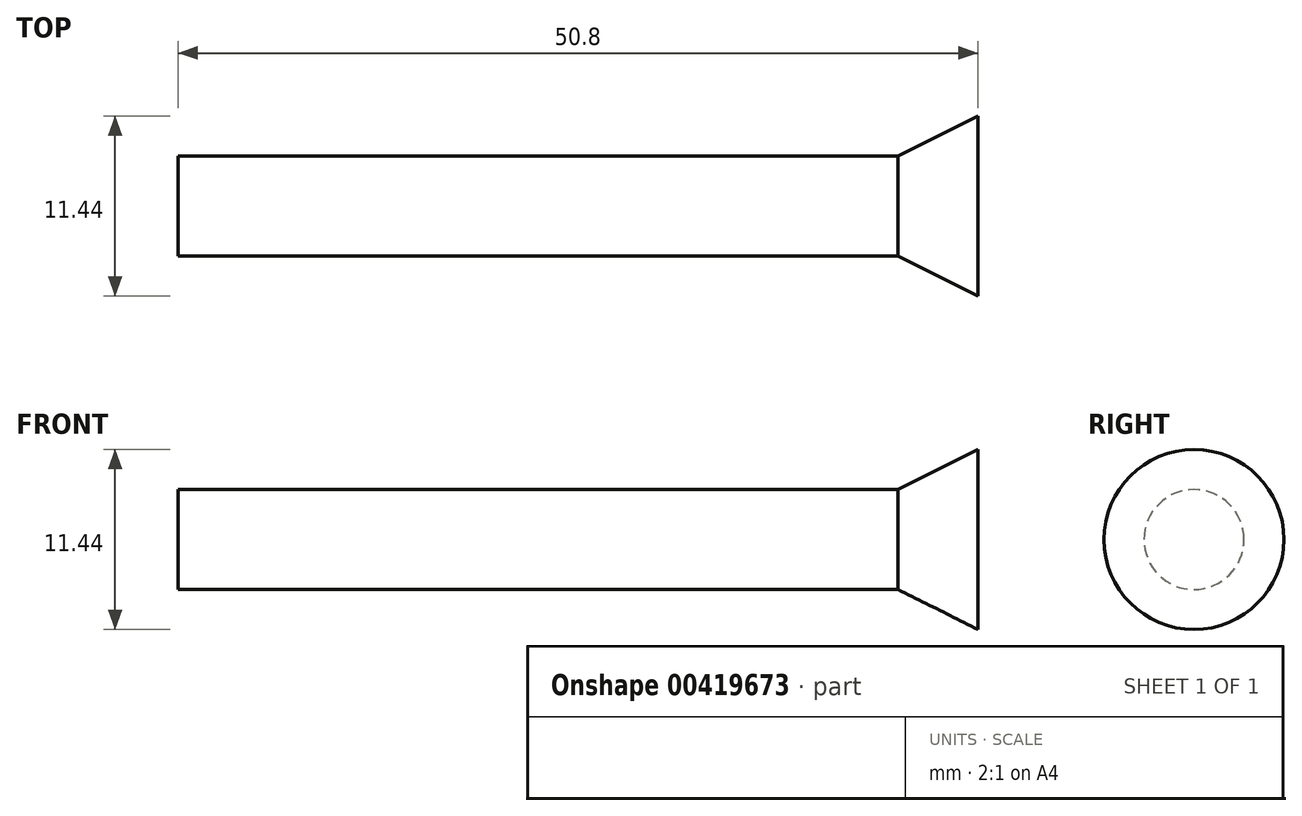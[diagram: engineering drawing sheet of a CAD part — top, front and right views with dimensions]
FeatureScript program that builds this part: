
annotation { "Feature Type Name" : "Feature", "Feature Type Description" : "" }
export const myFeature = defineFeature(function(context is Context, id is Id, definition is map)
    precondition{}
    {
        {
            var Q0;
            Q0=qCreatedBy(makeId("Right.planeOp"),FACE);
            var sketch = newSketch(context, id + "F0", { "sketchPlane" : qUnion([Q0])});
            skCircle(sketch, "E0", {"center": v(0, 0) * mm, "radius": 3.18 * mm});
            skSolve(sketch);
        }
        {
            var Q0;
            Q0 = qSketchRegion(id + "F0", true);
            extrude(context, id + "F1", {"entities" : qUnion([Q0]), "depth" : 45.72 * mm, "offsetDistance" : 25.4 * mm});
        }
        {
            var Q0;
            Q0=qCreatedBy(makeId("Front.planeOp"),FACE);
            var sketch = newSketch(context, id + "F2", { "sketchPlane" : qUnion([Q0])});
            skLineSegment(sketch, "E1.0", {"start": v(45.72, 3.18) * mm, "end": v(45.72, -3.18) * mm});
            skLineSegment(sketch, "E2", {"start": v(45.72, 3.17) * mm, "end": v(50.8, 5.71) * mm});
            skLineSegment(sketch, "E3", {"start": v(50.8, 5.72) * mm, "end": v(50.8, 0) * mm});
            skLineSegment(sketch, "E4", {"start": v(50.8, 0) * mm, "end": v(45.72, 0) * mm});
            skLineSegment(sketch, "E5", {"start": v(45.72, 0) * mm, "end": v(45.72, 3.18) * mm});
            skSolve(sketch);
        }
        {
            var Q0;
            Q0=makeQuery(id+"F2.imprint","IMPRINT",FACE,{"disambiguationData":[TD([[makeQuery(id+"F2.imprint","IMPRINT",EDGE,{"derivedFrom":sQuery(id+"F2.wireOp",EDGE,"E2")}),-1.0]])]});
            var Q1;
            Q1=sQuery(id+"F2.wireOp",EDGE,"E4");
            revolve(context, id + "F3", {"operationType" : NewBodyOperationType.ADD, "entities" : qUnion([Q0]), "axis" : qUnion([Q1]), "revolveType" : RevolveType.FULL});
        }
    });
